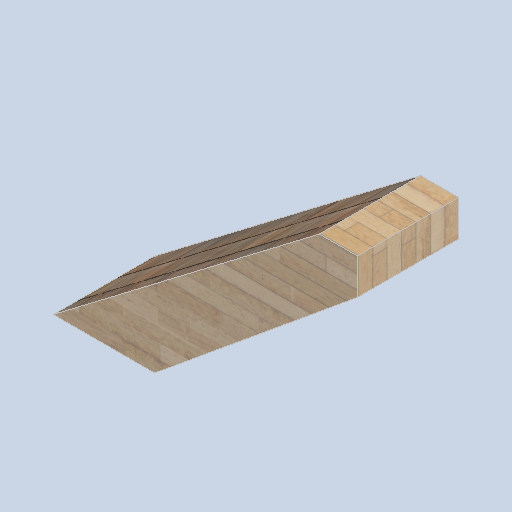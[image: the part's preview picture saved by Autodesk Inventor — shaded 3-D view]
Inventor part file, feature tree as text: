
AUTODESK INVENTOR PART (.ipt)
format: ipt  version: 2024.2 (Build 282272000, 272)  size: 321,024 bytes
history: native  units: mm
features: extrude x1, sketch x1
ambient origin geometry x8: Origin, YZ Plane, XZ Plane, XY Plane, X Axis, Y Axis, Z Axis, Center Point
bodies: Body1 (feature_tree)
feature tree (2):
  extrude  "Extrusion3"  Depth=400.0mm
  sketch  "Sketch1"  dims[d2=90.0deg d5=150.0mm d6=400.0mm d7=0.0mm]
